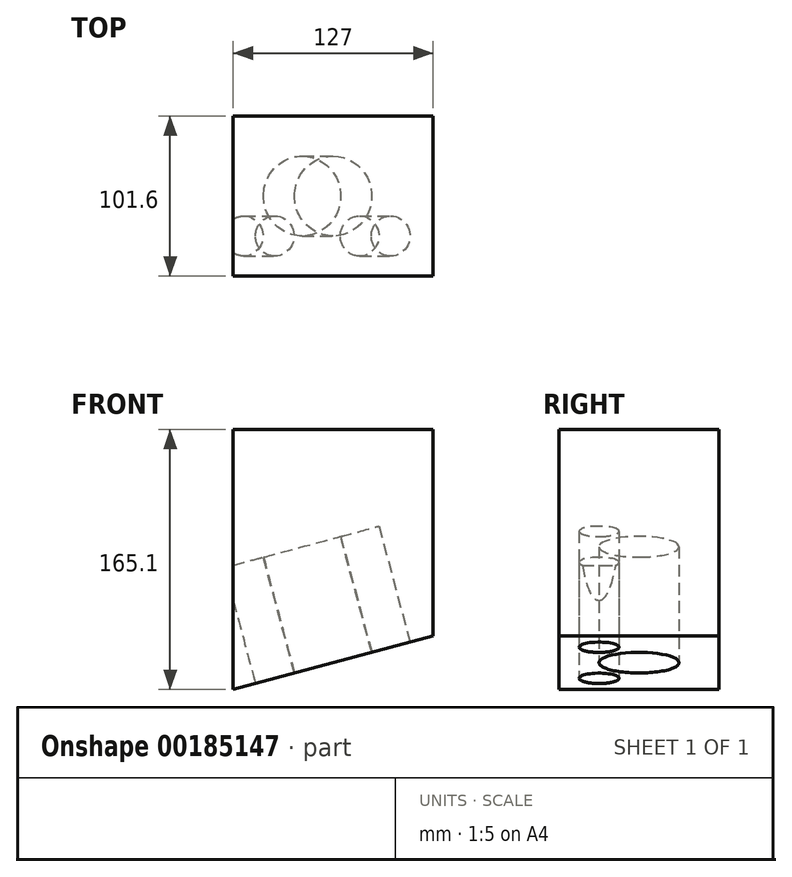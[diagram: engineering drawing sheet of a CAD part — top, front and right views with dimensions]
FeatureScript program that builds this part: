
annotation { "Feature Type Name" : "Feature", "Feature Type Description" : "" }
export const myFeature = defineFeature(function(context is Context, id is Id, definition is map)
    precondition{}
    {
        {
            var Q0;
            Q0=qCreatedBy(makeId("Front.planeOp"),FACE);
            var sketch = newSketch(context, id + "F0", { "sketchPlane" : qUnion([Q0])});
            skLineSegment(sketch, "E0", {"start": v(-50.8, 54.87) * mm, "end": v(-50.8, -110.23) * mm});
            skLineSegment(sketch, "E1", {"start": v(-50.8, -110.23) * mm, "end": v(76.2, -76.2) * mm});
            skLineSegment(sketch, "E2", {"start": v(76.2, -76.2) * mm, "end": v(76.2, 54.87) * mm});
            skLineSegment(sketch, "E3", {"start": v(76.2, 54.87) * mm, "end": v(-50.8, 54.87) * mm});
            skSolve(sketch);
        }
        {
            var Q0;
            Q0 = qSketchRegion(id + "F0", true);
            extrude(context, id + "F1", {"entities" : qUnion([Q0]), "depth" : 101.6 * mm});
        }
        {
            var Q0;
            Q0=makeQuery(id+"F1.opExtrude","SWEPT_FACE",FACE,{"disambiguationData":[OSD([sQuery(id+"F0.wireOp",EDGE,"E1")])]});
            var sketch = newSketch(context, id + "F2", { "sketchPlane" : qUnion([Q0])});
            skCircle(sketch, "E4", {"center": v(-11.86, 50.8) * mm, "radius": 25.4 * mm});
            skPoint(sketch, "E4.centerSnap0", {"position": v(-77.6, 50.8) * mm});
            skPoint(sketch, "E4.centerSnap1", {"position": v(-11.86, 101.6) * mm});
            skCircle(sketch, "E5", {"center": v(-50.26, 76.2) * mm, "radius": 12.7 * mm});
            skCircle(sketch, "E6", {"center": v(25.94, 76.2) * mm, "radius": 12.7 * mm});
            skSolve(sketch);
        }
        {
            var Q0;
            Q0 = qSketchRegion(id + "F2", true);
            extrude(context, id + "F3", {"entities" : qUnion([Q0]), "operationType" : NewBodyOperationType.REMOVE, "oppositeDirection" : true, "depth" : 76.2 * mm});
        }
    });
